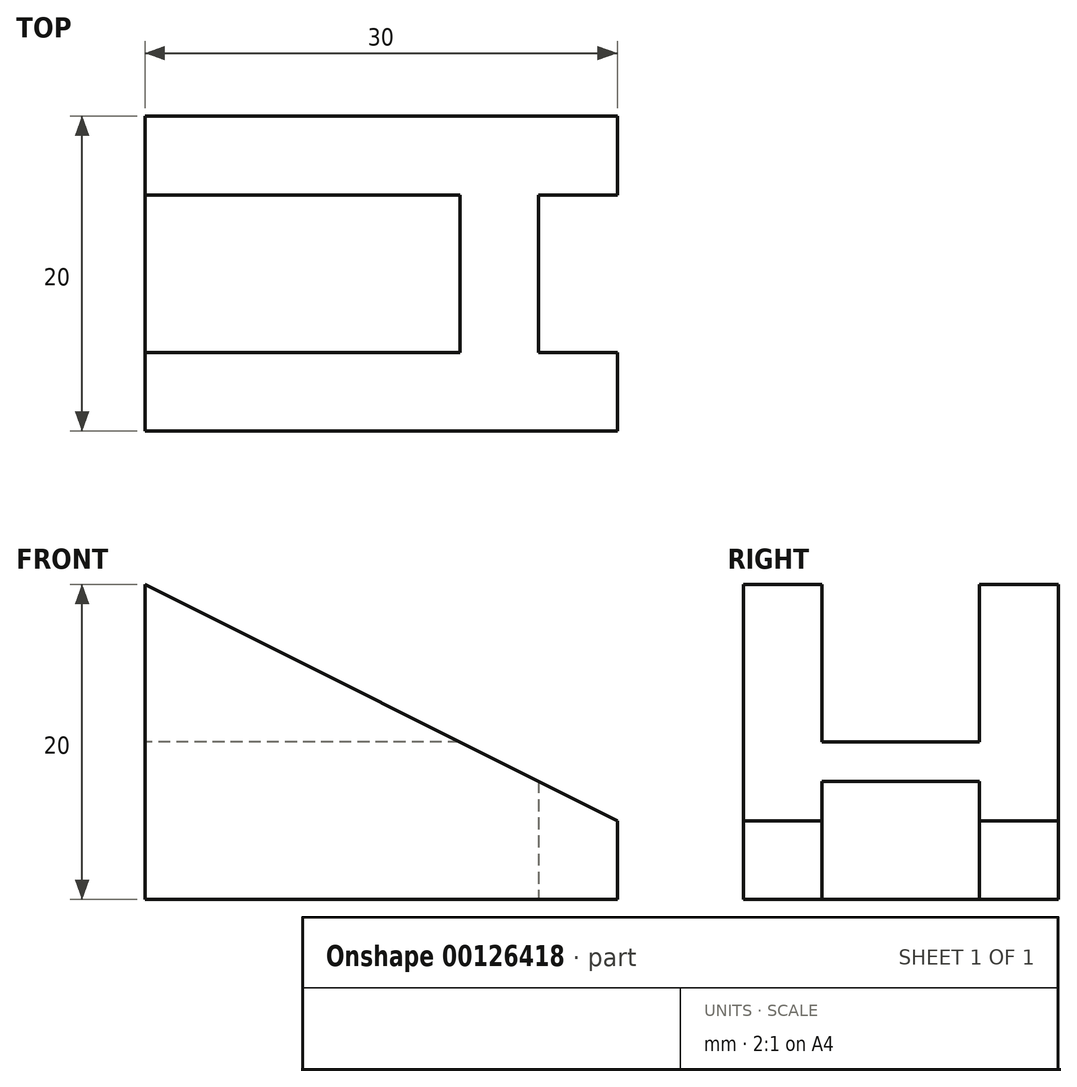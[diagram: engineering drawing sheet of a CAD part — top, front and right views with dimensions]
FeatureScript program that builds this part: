
annotation { "Feature Type Name" : "Feature", "Feature Type Description" : "" }
export const myFeature = defineFeature(function(context is Context, id is Id, definition is map)
    precondition{}
    {
        {
            var Q0;
            Q0=qCreatedBy(makeId("Top.planeOp"),FACE);
            var sketch = newSketch(context, id + "F0", { "sketchPlane" : qUnion([Q0])});
            skLineSegment(sketch, "E0", {"start": v(10, 0) * mm, "end": v(10, 5) * mm});
            skLineSegment(sketch, "E1", {"start": v(10, 5) * mm, "end": v(15, 5) * mm});
            skLineSegment(sketch, "E2", {"start": v(15, 5) * mm, "end": v(15, 10) * mm});
            skLineSegment(sketch, "E3", {"start": v(15, 10) * mm, "end": v(-15, 10) * mm});
            skLineSegment(sketch, "E4", {"start": v(-15, 10) * mm, "end": v(-15, -10) * mm});
            skLineSegment(sketch, "E5", {"start": v(-15, -10) * mm, "end": v(15, -10) * mm});
            skLineSegment(sketch, "E6", {"start": v(15, -10) * mm, "end": v(15, -5) * mm});
            skLineSegment(sketch, "E7", {"start": v(15, -5) * mm, "end": v(10, -5) * mm});
            skLineSegment(sketch, "E8", {"start": v(10, -5) * mm, "end": v(10, 0) * mm});
            skSolve(sketch);
        }
        {
            var Q0;
            Q0=makeQuery(id+"F0.imprint","IMPRINT",FACE,{"disambiguationData":[TD([[makeQuery(id+"F0.imprint","IMPRINT",EDGE,{"derivedFrom":sQuery(id+"F0.wireOp",EDGE,"E0")}),1.0]])]});
            extrude(context, id + "F1", {"entities" : qUnion([Q0]), "depth" : 20 * mm});
        }
        {
            var Q0;
            Q0=makeQuery(id+"F1.opExtrude","SWEPT_FACE",FACE,{"disambiguationData":[OSD([sQuery(id+"F0.wireOp",EDGE,"E5")])]});
            var sketch = newSketch(context, id + "F2", { "sketchPlane" : qUnion([Q0])});
            skLineSegment(sketch, "E9", {"start": v(15, 0) * mm, "end": v(15, 5) * mm});
            skLineSegment(sketch, "E10", {"start": v(15, 5) * mm, "end": v(-15, 20) * mm});
            skSolve(sketch);
        }
        {
            var Q0;
            Q0 = qSketchRegion(id + "F2", true);
            var Q1;
            {var subQ0=sQuery(id+"F2.wireOp",EDGE,"E10");Q1=makeQuery(id+"F2.imprint","IMPRINT",FACE,{"disambiguationData":[TD([[makeQuery(id+"F2.imprint","IMPRINT",EDGE,{"derivedFrom":subQ0}),-1.0]])]});}
            extrude(context, id + "F3", {"entities" : qUnion([Q0, Q1]), "operationType" : NewBodyOperationType.REMOVE, "oppositeDirection" : true, "depth" : 25 * mm});
        }
        {
            var Q0;
            Q0=makeQuery(id+"F1.opExtrude","SWEPT_FACE",FACE,{"disambiguationData":[OSD([sQuery(id+"F0.wireOp",EDGE,"E4")])]});
            var sketch = newSketch(context, id + "F4", { "sketchPlane" : qUnion([Q0])});
            skLineSegment(sketch, "E11", {"start": v(-10, 20) * mm, "end": v(-5, 20) * mm});
            skLineSegment(sketch, "E12", {"start": v(-5, 20) * mm, "end": v(-5, 10) * mm});
            skLineSegment(sketch, "E13", {"start": v(-5, 10) * mm, "end": v(5, 10) * mm});
            skLineSegment(sketch, "E14", {"start": v(5, 10) * mm, "end": v(5, 20) * mm});
            skLineSegment(sketch, "E15", {"start": v(5, 20) * mm, "end": v(10, 20) * mm});
            skSolve(sketch);
        }
        {
            var Q0;
            Q0 = qSketchRegion(id + "F4", true);
            var Q1;
            {var subQ0=sQuery(id+"F4.wireOp",EDGE,"E12");Q1=makeQuery(id+"F4.imprint","IMPRINT",FACE,{"disambiguationData":[TD([[makeQuery(id+"F4.imprint","IMPRINT",EDGE,{"derivedFrom":subQ0}),1.0]])]});}
            extrude(context, id + "F5", {"entities" : qUnion([Q0, Q1]), "operationType" : NewBodyOperationType.REMOVE, "oppositeDirection" : true, "depth" : 25 * mm});
        }
    });
